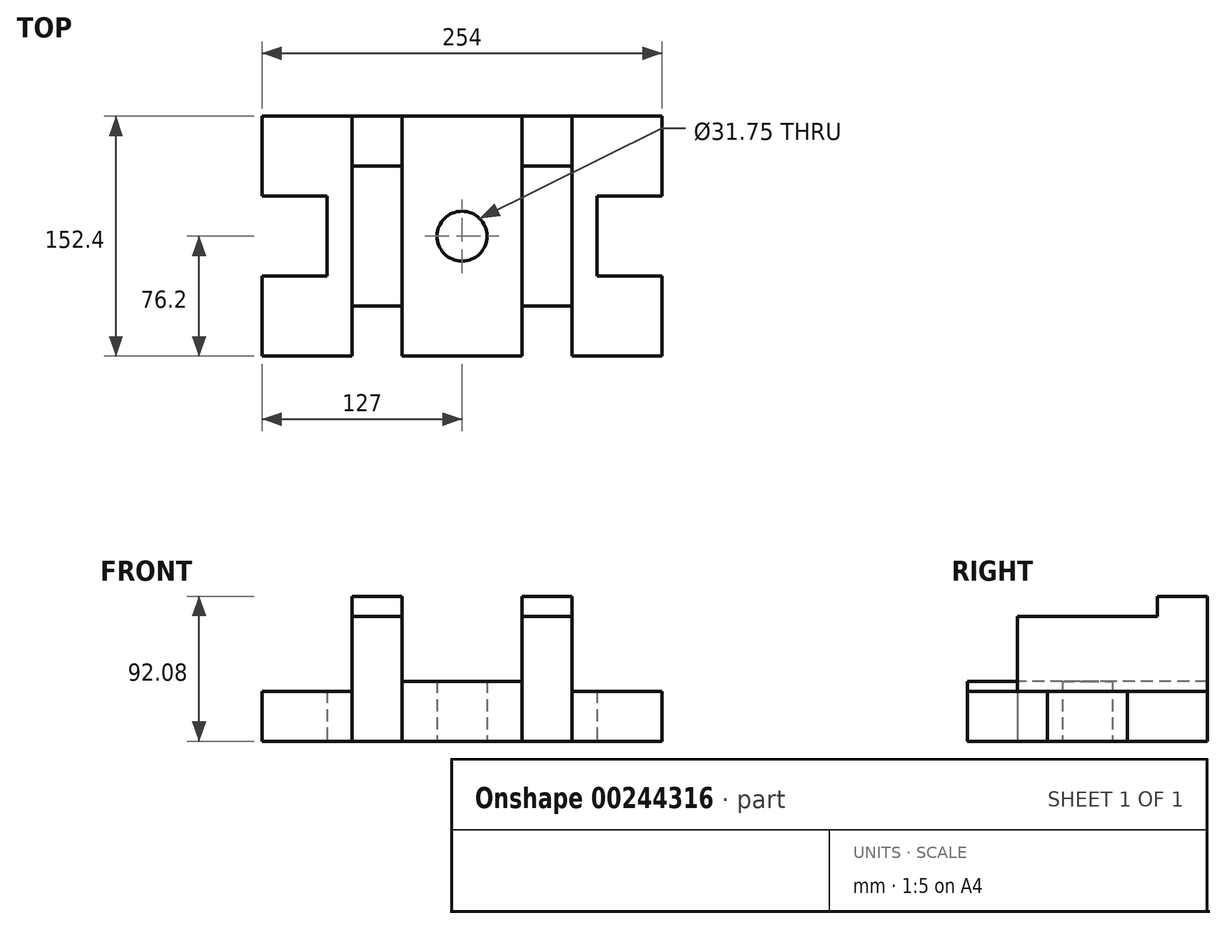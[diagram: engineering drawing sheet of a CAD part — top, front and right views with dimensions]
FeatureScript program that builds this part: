
annotation { "Feature Type Name" : "Feature", "Feature Type Description" : "" }
export const myFeature = defineFeature(function(context is Context, id is Id, definition is map)
    precondition{}
    {
        {
            var Q0;
            Q0=qCreatedBy(makeId("Top.planeOp"),FACE);
            var sketch = newSketch(context, id + "F0", { "sketchPlane" : qUnion([Q0])});
            skCircle(sketch, "E0", {"center": v(0, 0) * mm, "radius": 15.88 * mm});
            skLineSegment(sketch, "E1", {"start": v(0, 0) * mm, "end": v(0, -76.2) * mm});
            skLineSegment(sketch, "E2", {"start": v(0, 0) * mm, "end": v(0, 76.2) * mm});
            skPoint(sketch, "E3.MirrorCS.start.orphan", {"position": v(0, -76.2) * mm});
            skLineSegment(sketch, "E4", {"start": v(0, 76.2) * mm, "end": v(127, 76.2) * mm});
            skLineSegment(sketch, "E5", {"start": v(0, -76.2) * mm, "end": v(127, -76.2) * mm});
            skLineSegment(sketch, "E6", {"start": v(127, 76.2) * mm, "end": v(127, 25.4) * mm});
            skLineSegment(sketch, "E7", {"start": v(127, -76.2) * mm, "end": v(127, -25.4) * mm});
            skLineSegment(sketch, "E8", {"start": v(127, 25.4) * mm, "end": v(85.72, 25.4) * mm});
            skLineSegment(sketch, "E9", {"start": v(127, -25.4) * mm, "end": v(85.72, -25.4) * mm});
            skLineSegment(sketch, "E10", {"start": v(85.73, 25.4) * mm, "end": v(85.72, -25.4) * mm});
            skLineSegment(sketch, "E11", {"start": v(38.1, 44.45) * mm, "end": v(69.85, 44.45) * mm});
            skLineSegment(sketch, "E12", {"start": v(69.85, 44.45) * mm, "end": v(69.85, 76.2) * mm});
            skLineSegment(sketch, "E13", {"start": v(38.1, -76.2) * mm, "end": v(69.85, -76.2) * mm});
            skLineSegment(sketch, "E14", {"start": v(69.85, -76.2) * mm, "end": v(69.85, -44.45) * mm});
            skLineSegment(sketch, "E15", {"start": v(69.85, -44.45) * mm, "end": v(38.1, -44.45) * mm});
            skLineSegment(sketch, "E16", {"start": v(38.1, 76.2) * mm, "end": v(38.1, -76.2) * mm});
            skLineSegment(sketch, "E17", {"start": v(69.85, 44.45) * mm, "end": v(69.85, -44.45) * mm});
            skSolve(sketch);
        }
        {
            var Q0;
            {var subQ1=sQuery(id+"F0.wireOp",EDGE,"E6");Q0=makeQuery(id+"F0.imprint","IMPRINT",FACE,{"disambiguationData":[TD([[makeQuery(id+"F0.imprint","IMPRINT",EDGE,{"derivedFrom":subQ1}),-1.0]])]});}
            extrude(context, id + "F1", {"entities" : qUnion([Q0]), "depth" : 31.75 * mm});
        }
        {
            var Q0;
            {var subQ0=sQuery(id+"F0.wireOp",EDGE,"E13");Q0=makeQuery(id+"F0.imprint","IMPRINT",FACE,{"disambiguationData":[TD([[makeQuery(id+"F0.imprint","IMPRINT",EDGE,{"derivedFrom":subQ0}),1.0]])]});}
            var Q1;
            {var subQ4=sQuery(id+"F0.wireOp",EDGE,"E11");Q1=makeQuery(id+"F0.imprint","IMPRINT",FACE,{"disambiguationData":[TD([[makeQuery(id+"F0.imprint","IMPRINT",EDGE,{"derivedFrom":subQ4}),1.0]])]});}
            extrude(context, id + "F2", {"entities" : qUnion([Q0, Q1]), "operationType" : NewBodyOperationType.ADD, "depth" : 92.07 * mm});
        }
        {
            var Q0;
            {var subQ5=sQuery(id+"F0.wireOp",EDGE,"E0");var subQ8=sQuery(id+"F0.wireOp",EDGE,"E1");var subQ10=makeQuery(id+"F0.imprint","INTERSECT",VERTEX,{"derivedFrom":[subQ5,subQ8]});Q0=makeQuery(id+"F0.imprint","IMPRINT",FACE,{"disambiguationData":[TD([[makeQuery(id+"F0.imprint","IMPRINT",EDGE,{"disambiguationData":[TD([[subQ10,-1.0]])],"derivedFrom":subQ5}),-1.0]])]});}
            extrude(context, id + "F3", {"entities" : qUnion([Q0]), "operationType" : NewBodyOperationType.ADD, "depth" : 38.1 * mm});
        }
        {
            var Q0;
            {var subQ0=sQuery(id+"F0.wireOp",EDGE,"E11");Q0=makeQuery(id+"F0.imprint","IMPRINT",FACE,{"disambiguationData":[TD([[makeQuery(id+"F0.imprint","IMPRINT",EDGE,{"derivedFrom":subQ0}),-1.0]])]});}
            extrude(context, id + "F4", {"entities" : qUnion([Q0]), "operationType" : NewBodyOperationType.ADD, "depth" : 41.27 * mm});
        }
        {
            var Q0;
            {var subQ0=sQuery(id+"F0.wireOp",EDGE,"E11");Q0=makeQuery(id+"F0.imprint","IMPRINT",FACE,{"disambiguationData":[TD([[makeQuery(id+"F0.imprint","IMPRINT",EDGE,{"derivedFrom":subQ0}),-1.0]])]});}
            extrude(context, id + "F5", {"entities" : qUnion([Q0]), "operationType" : NewBodyOperationType.ADD, "depth" : 60.32 * mm});
        }
        {
            var Q0;
            Q0=makeQuery(id+"F5.opExtrude","CAP_FACE",FACE,{"disambiguationData":[OSD([sQuery(id+"F0.wireOp",EDGE,"E11"),sQuery(id+"F0.wireOp",EDGE,"E15"),sQuery(id+"F0.wireOp",EDGE,"E16"),sQuery(id+"F0.wireOp",EDGE,"E17")])],"isStart":false});
            extrude(context, id + "F6", {"entities" : qUnion([Q0]), "operationType" : NewBodyOperationType.ADD, "depth" : 19.05 * mm});
        }
        {
            var Q0;
            Q0=makeQuery(id+"F1.opExtrude","SWEPT_BODY",BODY,{"disambiguationData":[OSD([sQuery(id+"F0.wireOp",EDGE,"E4"),sQuery(id+"F0.wireOp",EDGE,"E5"),sQuery(id+"F0.wireOp",EDGE,"E6"),sQuery(id+"F0.wireOp",EDGE,"E7"),sQuery(id+"F0.wireOp",EDGE,"E8"),sQuery(id+"F0.wireOp",EDGE,"E9"),sQuery(id+"F0.wireOp",EDGE,"E10"),sQuery(id+"F0.wireOp",EDGE,"E12"),sQuery(id+"F0.wireOp",EDGE,"E14"),sQuery(id+"F0.wireOp",EDGE,"E17")])]});
            var Q1;
            Q1=makeQuery(id+"F3.opExtrude","SWEPT_FACE",FACE,{"disambiguationData":[OSD([sQuery(id+"F0.wireOp",EDGE,"E1")])]});
            mirror(context, id + "F7", {"operationType" : NewBodyOperationType.ADD, "entities" : qUnion([Q0]), "mirrorPlane" : qUnion([Q1])});
        }
    });
